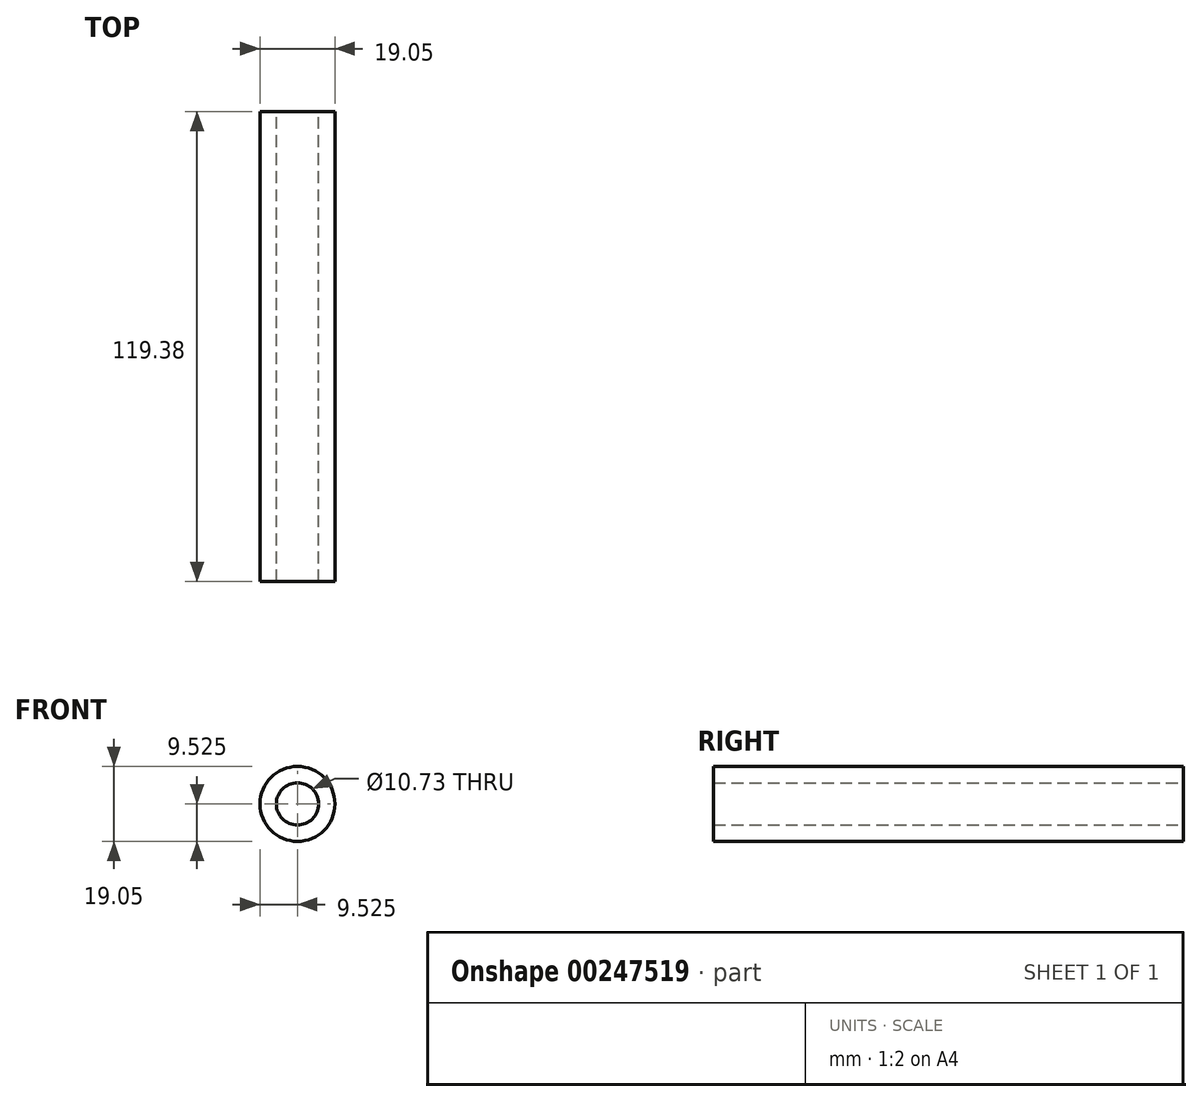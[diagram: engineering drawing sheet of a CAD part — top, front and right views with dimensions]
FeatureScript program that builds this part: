
annotation { "Feature Type Name" : "Feature", "Feature Type Description" : "" }
export const myFeature = defineFeature(function(context is Context, id is Id, definition is map)
    precondition{}
    {
        {
            var Q0;
            Q0=qCreatedBy(makeId("Front.planeOp"),FACE);
            var sketch = newSketch(context, id + "F0", { "sketchPlane" : qUnion([Q0])});
            skCircle(sketch, "E0", {"center": v(-22.12, 43.74) * mm, "radius": 9.53 * mm});
            skCircle(sketch, "E1", {"center": v(-22.12, 43.74) * mm, "radius": 5.36 * mm});
            skSolve(sketch);
        }
        {
            var Q0;
            Q0 = qSketchRegion(id + "F0", true);
            extrude(context, id + "F1", {"entities" : qUnion([Q0]), "depth" : 119.38 * mm});
        }
    });
